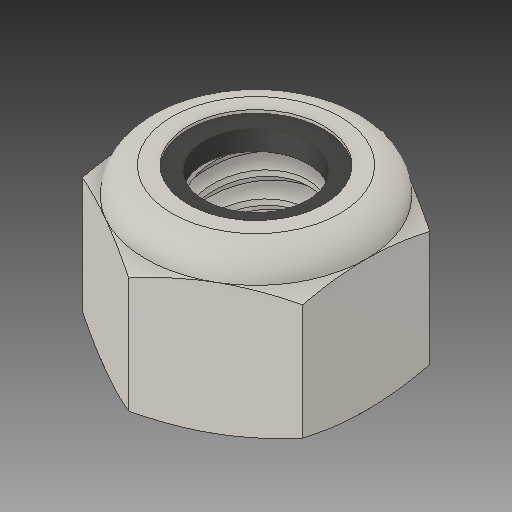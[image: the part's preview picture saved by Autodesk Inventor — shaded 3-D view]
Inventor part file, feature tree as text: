
AUTODESK INVENTOR PART (.ipt)
format: ipt  version: 2017 (Build 210142000, 142)  size: 295,936 bytes
history: native  units: in
note: dims shown in document units (in); Inventor stores cm internally (conversion verified against a paired STEP export)
features: other x1, revolve x1
ambient origin geometry x8: Origin, YZ Plane, XZ Plane, XY Plane, X Axis, Y Axis, Z Axis, Center Point
bodies: Solid1 (feature_tree), Solid2 (feature_tree)
feature tree (2):
  other  "Cut-Revolve4"
  revolve  "Revolve2"  [1 undecoded]
note: 1 required parameter value undecoded (feature->parameter linkage not recoverable at this tier; creation-order binding heuristic only, values carry confidence <= 0.55)
